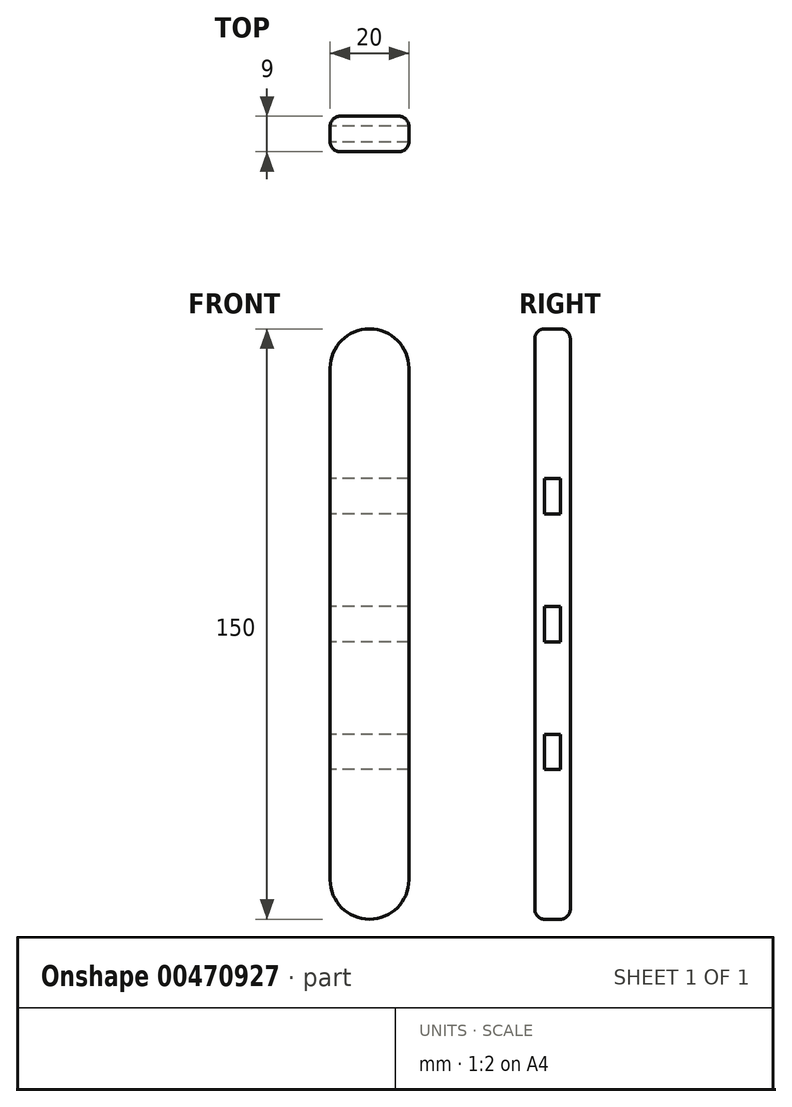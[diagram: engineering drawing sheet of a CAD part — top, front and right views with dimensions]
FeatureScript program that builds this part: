
annotation { "Feature Type Name" : "Feature", "Feature Type Description" : "" }
export const myFeature = defineFeature(function(context is Context, id is Id, definition is map)
    precondition{}
    {
        {
            var Q0;
            Q0=qCreatedBy(makeId("Front.planeOp"),FACE);
            var sketch = newSketch(context, id + "F0", { "sketchPlane" : qUnion([Q0])});
            skLineSegment(sketch, "E0", {"start": v(-35.76, 76.93) * mm, "end": v(-15.76, 76.93) * mm});
            skLineSegment(sketch, "E1", {"start": v(-15.76, 76.93) * mm, "end": v(-15.76, -73.07) * mm});
            skLineSegment(sketch, "E2", {"start": v(-15.76, -73.07) * mm, "end": v(-35.76, -73.07) * mm});
            skLineSegment(sketch, "E3", {"start": v(-35.76, -73.07) * mm, "end": v(-35.76, 76.93) * mm});
            skSolve(sketch);
        }
        {
            var Q0;
            Q0=makeQuery(id+"F0.imprint","IMPRINT",FACE,{"disambiguationData":[TD([[makeQuery(id+"F0.imprint","IMPRINT",EDGE,{"derivedFrom":sQuery(id+"F0.wireOp",EDGE,"E0")}),-1.0]])]});
            extrude(context, id + "F1", {"entities" : qUnion([Q0]), "depth" : 5 * mm});
        }
        {
            var Q0;
            Q0=makeQuery(id+"F1.opExtrude","SWEPT_EDGE",EDGE,{"disambiguationData":[OSD([sQuery(id+"F0.wireOp",EDGE,"E0"),sQuery(id+"F0.wireOp",EDGE,"E3")])]});
            var Q1;
            Q1=makeQuery(id+"F1.opExtrude","SWEPT_EDGE",EDGE,{"disambiguationData":[OSD([sQuery(id+"F0.wireOp",EDGE,"E0"),sQuery(id+"F0.wireOp",EDGE,"E1")])]});
            var Q2;
            Q2=makeQuery(id+"F1.opExtrude","SWEPT_EDGE",EDGE,{"disambiguationData":[OSD([sQuery(id+"F0.wireOp",EDGE,"E1"),sQuery(id+"F0.wireOp",EDGE,"E2")])]});
            var Q3;
            Q3=makeQuery(id+"F1.opExtrude","SWEPT_EDGE",EDGE,{"disambiguationData":[OSD([sQuery(id+"F0.wireOp",EDGE,"E2"),sQuery(id+"F0.wireOp",EDGE,"E3")])]});
            fillet(context, id + "F2", {"entities" : qUnion([Q0, Q1, Q2, Q3]), "radius" : 10 * mm, "tangentPropagation" : true, "allowEdgeOverflow" : false});
        }
        {
            var Q0;
            Q0=makeQuery(id+"F1.opExtrude","SWEPT_FACE",FACE,{"disambiguationData":[OSD([sQuery(id+"F0.wireOp",EDGE,"E3")])]});
            var sketch = newSketch(context, id + "F3", { "sketchPlane" : qUnion([Q0])});
            skLineSegment(sketch, "E4", {"start": v(5, 1.93) * mm, "end": v(5, -3.07) * mm});
            skLineSegment(sketch, "E5", {"start": v(5, -3.07) * mm, "end": v(5, 1.93) * mm});
            skLineSegment(sketch, "E6", {"start": v(5, 1.93) * mm, "end": v(5, 6.93) * mm});
            skLineSegment(sketch, "E7", {"start": v(5, 6.93) * mm, "end": v(0, 6.93) * mm});
            skLineSegment(sketch, "E8", {"start": v(0, 6.93) * mm, "end": v(0, 1.93) * mm});
            skLineSegment(sketch, "E9", {"start": v(0, 1.93) * mm, "end": v(0, -3.07) * mm});
            skLineSegment(sketch, "E10", {"start": v(0, -3.07) * mm, "end": v(5, -3.07) * mm});
            skLineSegment(sketch, "E11", {"start": v(0.5, 1.93) * mm, "end": v(0.5, 6.43) * mm});
            skLineSegment(sketch, "E12", {"start": v(0.5, 6.43) * mm, "end": v(4.5, 6.43) * mm});
            skLineSegment(sketch, "E13", {"start": v(4.5, 6.43) * mm, "end": v(4.5, -2.57) * mm});
            skLineSegment(sketch, "E14", {"start": v(4.5, -2.57) * mm, "end": v(0.5, -2.57) * mm});
            skLineSegment(sketch, "E15", {"start": v(0.5, -2.57) * mm, "end": v(0.5, 1.93) * mm});
            skPoint(sketch, "E16.end.orphan", {"position": v(2.5, 6.43) * mm});
            skPoint(sketch, "E16.start.orphan", {"position": v(2.5, 6.93) * mm});
            skPoint(sketch, "E17.end.orphan", {"position": v(4.5, 1.93) * mm});
            skPoint(sketch, "E18.end.orphan", {"position": v(2.5, -2.57) * mm});
            skPoint(sketch, "E18.start.orphan", {"position": v(2.5, -3.07) * mm});
            skSolve(sketch);
        }
        {
            var Q0;
            Q0=makeQuery(id+"F3.imprint","IMPRINT",FACE,{"disambiguationData":[TD([[makeQuery(id+"F3.imprint","IMPRINT",EDGE,{"derivedFrom":sQuery(id+"F3.wireOp",EDGE,"E11")}),-1.0]])]});
            extrude(context, id + "F4", {"entities" : qUnion([Q0]), "operationType" : NewBodyOperationType.REMOVE, "oppositeDirection" : true, "depth" : 20 * mm});
        }
        {
            var Q0;
            Q0=makeQuery(id+"F1.opExtrude","SWEPT_FACE",FACE,{"disambiguationData":[OSD([sQuery(id+"F0.wireOp",EDGE,"E3")])]});
            var sketch = newSketch(context, id + "F5", { "sketchPlane" : qUnion([Q0])});
            skLineSegment(sketch, "E19", {"start": v(5, 66.93) * mm, "end": v(5, 1.93) * mm});
            skLineSegment(sketch, "E20", {"start": v(5, 1.93) * mm, "end": v(5, -63.07) * mm});
            skLineSegment(sketch, "E21", {"start": v(0, -30.57) * mm, "end": v(0, -25.57) * mm});
            skLineSegment(sketch, "E22", {"start": v(0, -25.57) * mm, "end": v(5, -25.57) * mm});
            skLineSegment(sketch, "E23", {"start": v(5, -25.57) * mm, "end": v(5, -30.57) * mm});
            skLineSegment(sketch, "E24", {"start": v(0, -30.57) * mm, "end": v(0, -35.57) * mm});
            skLineSegment(sketch, "E25", {"start": v(0, -35.57) * mm, "end": v(5, -35.57) * mm});
            skLineSegment(sketch, "E26", {"start": v(5, -35.57) * mm, "end": v(5, -30.57) * mm});
            skLineSegment(sketch, "E27", {"start": v(2.5, -35.07) * mm, "end": v(0.5, -35.07) * mm});
            skLineSegment(sketch, "E28", {"start": v(0.5, -35.07) * mm, "end": v(0.5, -26.07) * mm});
            skLineSegment(sketch, "E29", {"start": v(0.5, -26.07) * mm, "end": v(4.5, -26.07) * mm});
            skLineSegment(sketch, "E30", {"start": v(4.5, -26.07) * mm, "end": v(4.5, -35.07) * mm});
            skLineSegment(sketch, "E31", {"start": v(4.5, -35.07) * mm, "end": v(2.5, -35.07) * mm});
            skPoint(sketch, "E32.end.orphan", {"position": v(2.5, -26.07) * mm});
            skPoint(sketch, "E32.start.orphan", {"position": v(2.5, -25.57) * mm});
            skPoint(sketch, "E33.end.orphan", {"position": v(0.5, -30.57) * mm});
            skPoint(sketch, "E34.end.orphan", {"position": v(4.5, -30.57) * mm});
            skPoint(sketch, "E35.start.orphan", {"position": v(2.5, -35.57) * mm});
            skLineSegment(sketch, "E36", {"start": v(0, 34.43) * mm, "end": v(0, 29.43) * mm});
            skLineSegment(sketch, "E37", {"start": v(0, 29.43) * mm, "end": v(5, 29.43) * mm});
            skLineSegment(sketch, "E38", {"start": v(5, 29.43) * mm, "end": v(5, 34.43) * mm});
            skLineSegment(sketch, "E39", {"start": v(0, 34.43) * mm, "end": v(0, 39.43) * mm});
            skLineSegment(sketch, "E40", {"start": v(0, 39.43) * mm, "end": v(5, 39.43) * mm});
            skLineSegment(sketch, "E41", {"start": v(5, 39.43) * mm, "end": v(5, 34.43) * mm});
            skLineSegment(sketch, "E42", {"start": v(5, 34.43) * mm, "end": v(5, 39.43) * mm});
            skLineSegment(sketch, "E43", {"start": v(5, 34.43) * mm, "end": v(5, 29.43) * mm});
            skLineSegment(sketch, "E44", {"start": v(0.5, 34.43) * mm, "end": v(0.5, 38.93) * mm});
            skLineSegment(sketch, "E45", {"start": v(0.5, 38.93) * mm, "end": v(4.5, 38.93) * mm});
            skLineSegment(sketch, "E46", {"start": v(4.5, 38.93) * mm, "end": v(4.5, 29.93) * mm});
            skLineSegment(sketch, "E47", {"start": v(4.5, 29.93) * mm, "end": v(0.5, 29.93) * mm});
            skLineSegment(sketch, "E48", {"start": v(0.5, 29.93) * mm, "end": v(0.5, 34.43) * mm});
            skPoint(sketch, "E49.end.orphan", {"position": v(2.5, 38.93) * mm});
            skPoint(sketch, "E49.start.orphan", {"position": v(2.5, 39.43) * mm});
            skPoint(sketch, "E50.end.orphan", {"position": v(4.5, 34.43) * mm});
            skPoint(sketch, "E51.end.orphan", {"position": v(2.5, 29.93) * mm});
            skPoint(sketch, "E51.start.orphan", {"position": v(2.5, 29.43) * mm});
            skSolve(sketch);
        }
        {
            var Q0;
            Q0=makeQuery(id+"F5.imprint","IMPRINT",FACE,{"disambiguationData":[TD([[makeQuery(id+"F5.imprint","IMPRINT",EDGE,{"derivedFrom":sQuery(id+"F5.wireOp",EDGE,"E27")}),-1.0]])]});
            var Q1;
            Q1=makeQuery(id+"F5.imprint","IMPRINT",FACE,{"disambiguationData":[TD([[makeQuery(id+"F5.imprint","IMPRINT",EDGE,{"derivedFrom":sQuery(id+"F5.wireOp",EDGE,"E44")}),-1.0]])]});
            extrude(context, id + "F6", {"entities" : qUnion([Q0, Q1]), "operationType" : NewBodyOperationType.REMOVE, "oppositeDirection" : true, "depth" : 20 * mm});
        }
        {
            var Q0;
            Q0=makeQuery(id+"F1.opExtrude","CAP_FACE",FACE,{"disambiguationData":[OSD([sQuery(id+"F0.wireOp",EDGE,"E0"),sQuery(id+"F0.wireOp",EDGE,"E1"),sQuery(id+"F0.wireOp",EDGE,"E2"),sQuery(id+"F0.wireOp",EDGE,"E3")])],"isStart":true});
            extrude(context, id + "F7", {"entities" : qUnion([Q0]), "operationType" : NewBodyOperationType.ADD, "depth" : 2 * mm});
        }
        {
            var Q0;
            Q0=makeQuery(id+"F1.opExtrude","CAP_FACE",FACE,{"disambiguationData":[OSD([sQuery(id+"F0.wireOp",EDGE,"E0"),sQuery(id+"F0.wireOp",EDGE,"E1"),sQuery(id+"F0.wireOp",EDGE,"E2"),sQuery(id+"F0.wireOp",EDGE,"E3")])],"isStart":false});
            extrude(context, id + "F8", {"entities" : qUnion([Q0]), "operationType" : NewBodyOperationType.ADD, "depth" : 2 * mm});
        }
        {
            var Q0;
            Q0=makeQuery(id+"FHfORTTBxeLGeVu_1.boolean.opBoolean","COPY",FACE,{"derivedFrom":makeQuery(id+"FHfORTTBxeLGeVu_1.opExtrude","SWEPT_FACE",FACE,{"disambiguationData":[OSD([sQuery(id+"F0fAoiaGvUpmX24_1.wireOp",EDGE,"Pp1HHsye-YvLG-8qyb-Xq0n-zQea7nWq2jnU")])]})});
            var Q1;
            Q1=makeQuery(id+"F8.opExtrude","CAP_FACE",FACE,{"disambiguationData":[OSD([sQuery(id+"F0.wireOp",EDGE,"E0"),sQuery(id+"F0.wireOp",EDGE,"E1"),sQuery(id+"F0.wireOp",EDGE,"E2"),sQuery(id+"F0.wireOp",EDGE,"E3")])],"isStart":false});
            var Q2;
            Q2=makeQuery(id+"F7.opExtrude","CAP_FACE",FACE,{"disambiguationData":[OSD([sQuery(id+"F0.wireOp",EDGE,"E0"),sQuery(id+"F0.wireOp",EDGE,"E1"),sQuery(id+"F0.wireOp",EDGE,"E2"),sQuery(id+"F0.wireOp",EDGE,"E3")])],"isStart":false});
            fillet(context, id + "F9", {"entities" : qUnion([Q0, Q1, Q2]), "radius" : 2.5 * mm, "tangentPropagation" : true, "allowEdgeOverflow" : false});
        }
    });
